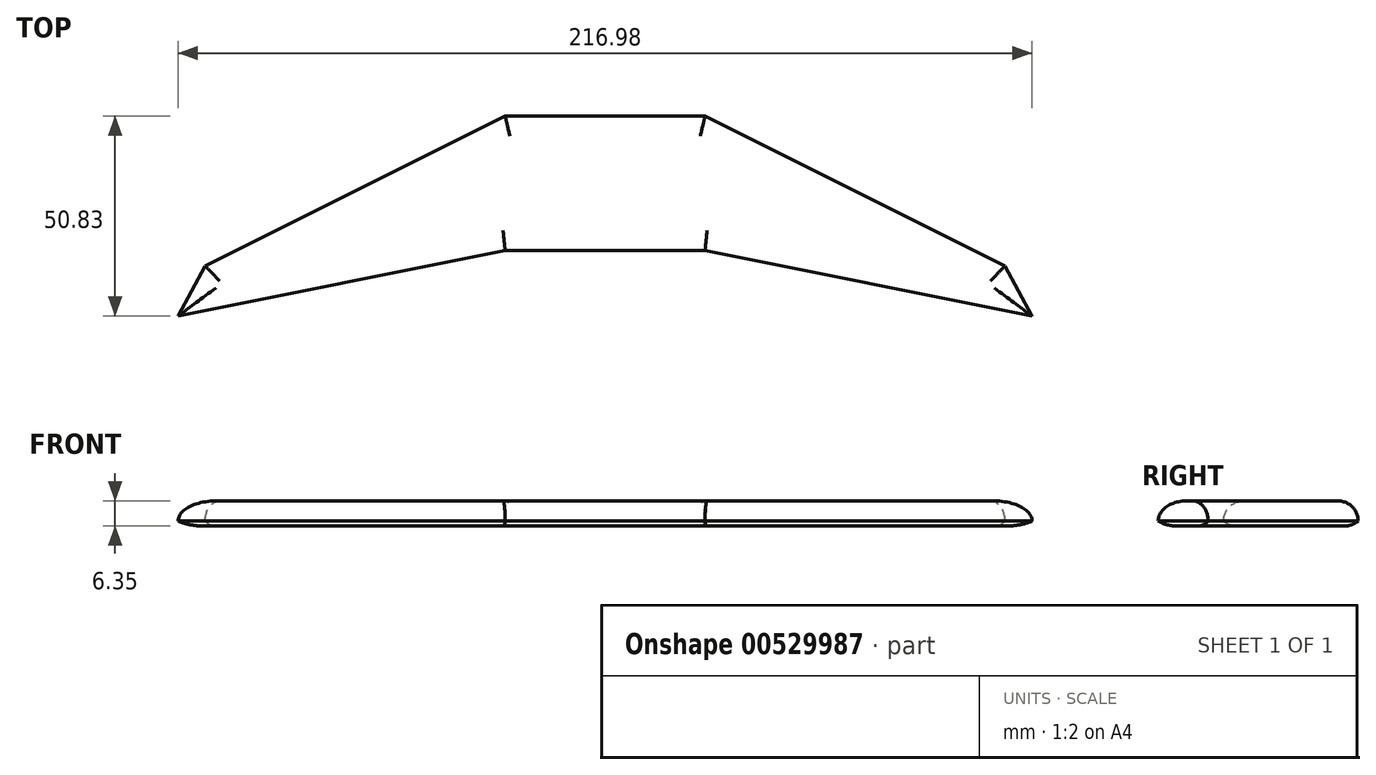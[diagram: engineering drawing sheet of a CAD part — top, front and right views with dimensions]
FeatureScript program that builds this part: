
annotation { "Feature Type Name" : "Feature", "Feature Type Description" : "" }
export const myFeature = defineFeature(function(context is Context, id is Id, definition is map)
    precondition{}
    {
        {
            var Q0;
            Q0=qCreatedBy(makeId("Top.planeOp"),FACE);
            var sketch = newSketch(context, id + "F0", { "sketchPlane" : qUnion([Q0])});
            skLineSegment(sketch, "E0", {"start": v(-25.4, 0) * mm, "end": v(25.4, 0) * mm});
            skLineSegment(sketch, "E1", {"start": v(-25.4, 0) * mm, "end": v(-101.6, -38.1) * mm});
            skLineSegment(sketch, "E2", {"start": v(25.4, 0) * mm, "end": v(101.6, -38.1) * mm});
            skLineSegment(sketch, "E3", {"start": v(-101.6, -38.1) * mm, "end": v(-108.5, -50.83) * mm});
            skLineSegment(sketch, "E4", {"start": v(101.6, -38.1) * mm, "end": v(108.5, -50.83) * mm});
            skLineSegment(sketch, "E5", {"start": v(-108.5, -50.83) * mm, "end": v(-25.4, -34.2) * mm});
            skLineSegment(sketch, "E6", {"start": v(108.5, -50.83) * mm, "end": v(25.4, -34.2) * mm});
            skLineSegment(sketch, "E7", {"start": v(-25.4, -34.2) * mm, "end": v(25.4, -34.2) * mm});
            skSolve(sketch);
        }
        {
            var Q0;
            Q0=makeQuery(id+"F0.imprint","IMPRINT",FACE,{"disambiguationData":[TD([[makeQuery(id+"F0.imprint","IMPRINT",EDGE,{"derivedFrom":sQuery(id+"F0.wireOp",EDGE,"E0")}),-1.0]])]});
            extrude(context, id + "F1", {"entities" : qUnion([Q0]), "depth" : 6.35 * mm, "offsetDistance" : 25.4 * mm});
        }
        {
            var Q0;
            Q0=makeQuery(id+"F1.opExtrude","CAP_FACE",FACE,{"disambiguationData":[OSD([sQuery(id+"F0.wireOp",EDGE,"E0"),sQuery(id+"F0.wireOp",EDGE,"E1"),sQuery(id+"F0.wireOp",EDGE,"E2"),sQuery(id+"F0.wireOp",EDGE,"E3"),sQuery(id+"F0.wireOp",EDGE,"E4"),sQuery(id+"F0.wireOp",EDGE,"E5"),sQuery(id+"F0.wireOp",EDGE,"E6"),sQuery(id+"F0.wireOp",EDGE,"E7")])],"isStart":false});
            fillet(context, id + "F2", {"entities" : qUnion([Q0]), "radius" : 5.08 * mm, "tangentPropagation" : true, "allowEdgeOverflow" : false});
        }
        {
            var Q0;
            Q0=makeQuery(id+"F1.opExtrude","CAP_FACE",FACE,{"disambiguationData":[OSD([sQuery(id+"F0.wireOp",EDGE,"E0"),sQuery(id+"F0.wireOp",EDGE,"E1"),sQuery(id+"F0.wireOp",EDGE,"E2"),sQuery(id+"F0.wireOp",EDGE,"E3"),sQuery(id+"F0.wireOp",EDGE,"E4"),sQuery(id+"F0.wireOp",EDGE,"E5"),sQuery(id+"F0.wireOp",EDGE,"E6"),sQuery(id+"F0.wireOp",EDGE,"E7")])],"isStart":true});
            fillet(context, id + "F3", {"entities" : qUnion([Q0]), "radius" : 5.08 * mm, "tangentPropagation" : true, "allowEdgeOverflow" : false});
        }
    });
